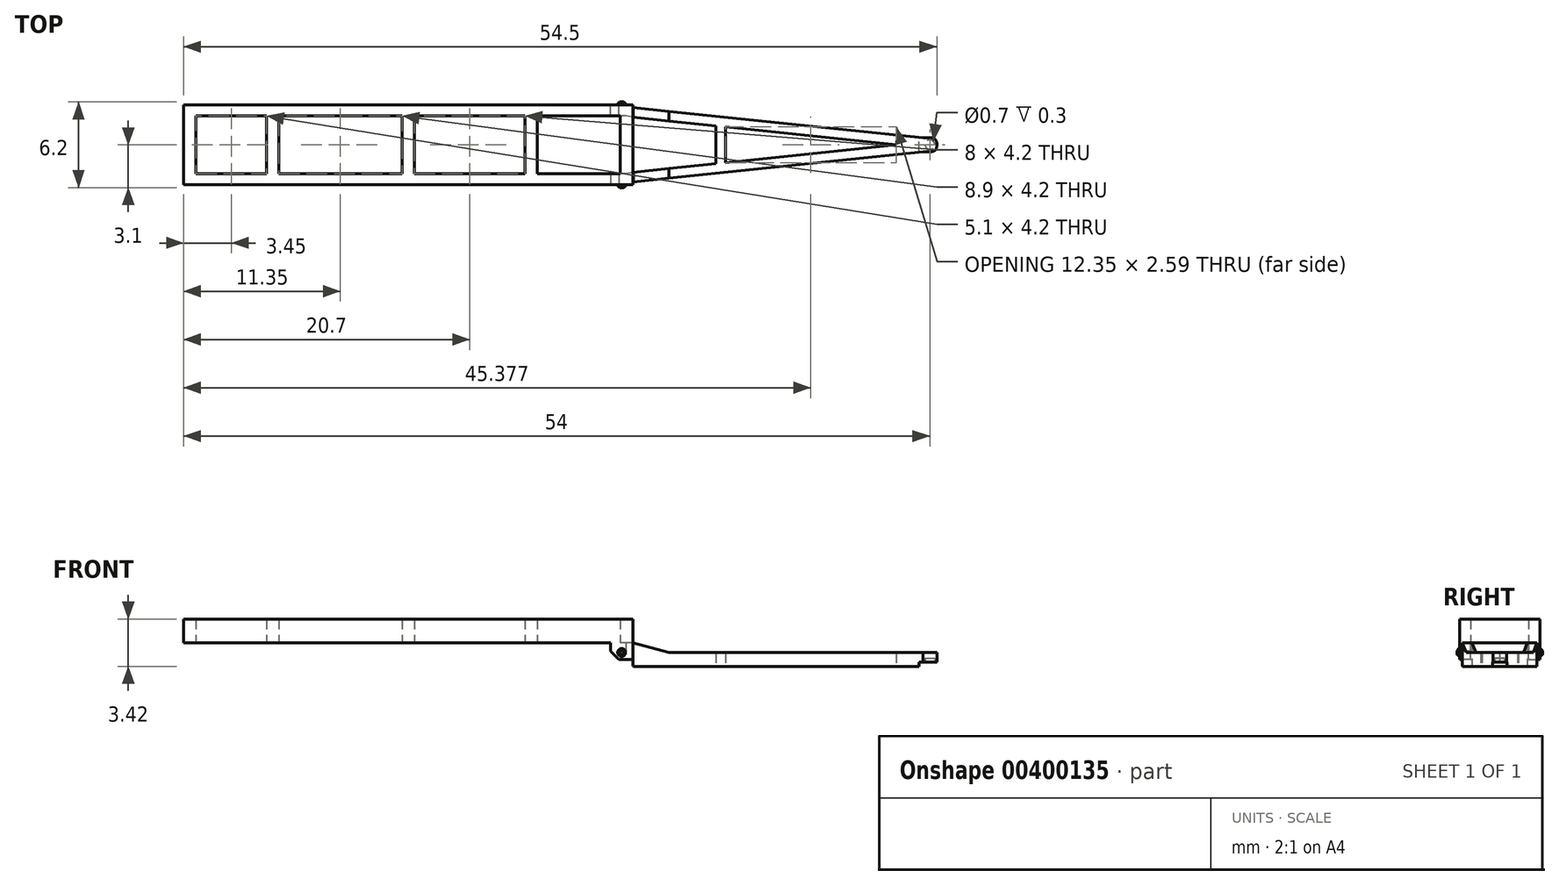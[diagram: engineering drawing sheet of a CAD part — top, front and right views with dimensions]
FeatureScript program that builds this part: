
annotation { "Feature Type Name" : "Feature", "Feature Type Description" : "" }
export const myFeature = defineFeature(function(context is Context, id is Id, definition is map)
    precondition{}
    {
        {
            var Q0;
            Q0=qCreatedBy(makeId("Top.planeOp"),FACE);
            var sketch = newSketch(context, id + "F0", { "sketchPlane" : qUnion([Q0])});
            skLineSegment(sketch, "E0", {"start": v(0, 0) * mm, "end": v(0, -2.9) * mm});
            skLineSegment(sketch, "E1", {"start": v(0, -2.9) * mm, "end": v(32.5, -2.9) * mm});
            skLineSegment(sketch, "E2", {"start": v(31.6, -2.1) * mm, "end": v(25.6, -2.1) * mm});
            skLineSegment(sketch, "E3", {"start": v(0.9, -2.1) * mm, "end": v(0.9, 0) * mm});
            skLineSegment(sketch, "E4", {"start": v(0.9, 0) * mm, "end": v(0, 0) * mm});
            skLineSegment(sketch, "E5", {"start": v(6, -2.1) * mm, "end": v(6, 0) * mm});
            skLineSegment(sketch, "E6", {"start": v(6, 0) * mm, "end": v(6.9, 0) * mm});
            skLineSegment(sketch, "E7", {"start": v(6.9, 0) * mm, "end": v(6.9, -2.1) * mm});
            skLineSegment(sketch, "E8.trimOffspring", {"start": v(6, -2.1) * mm, "end": v(0.9, -2.1) * mm});
            skLineSegment(sketch, "E9", {"start": v(32.5, -2.9) * mm, "end": v(32.5, 0) * mm});
            skLineSegment(sketch, "E10", {"start": v(32.5, 0) * mm, "end": v(31.6, 0) * mm});
            skLineSegment(sketch, "E11", {"start": v(31.6, 0) * mm, "end": v(31.6, -2.1) * mm});
            skLineSegment(sketch, "E12", {"start": v(25.6, -2.1) * mm, "end": v(25.6, 0) * mm});
            skLineSegment(sketch, "E13", {"start": v(25.6, 0) * mm, "end": v(24.7, 0) * mm});
            skLineSegment(sketch, "E14", {"start": v(24.7, 0) * mm, "end": v(24.7, -2.1) * mm});
            skLineSegment(sketch, "E15.trimOffspring", {"start": v(24.7, -2.1) * mm, "end": v(16.7, -2.1) * mm});
            skLineSegment(sketch, "E16", {"start": v(15.8, -2.1) * mm, "end": v(15.8, 0) * mm});
            skLineSegment(sketch, "E17", {"start": v(15.8, 0) * mm, "end": v(16.7, 0) * mm});
            skLineSegment(sketch, "E18", {"start": v(16.7, 0) * mm, "end": v(16.7, -2.1) * mm});
            skLineSegment(sketch, "E19.trimOffspring", {"start": v(15.8, -2.1) * mm, "end": v(6.9, -2.1) * mm});
            skSolve(sketch);
        }
        {
            var Q0;
            Q0 = qSketchRegion(id + "F0", true);
            extrude(context, id + "F1", {"entities" : qUnion([Q0]), "depth" : 1.72 * mm});
        }
        {
            var Q0;
            Q0=makeQuery(id+"F1.opExtrude","SWEPT_FACE",FACE,{"disambiguationData":[OSD([sQuery(id+"F0.wireOp",EDGE,"E1")])]});
            var sketch = newSketch(context, id + "F2", { "sketchPlane" : qUnion([Q0])});
            skLineSegment(sketch, "E20", {"start": v(30.9, -0.6) * mm, "end": v(32, -1.7) * mm});
            skLineSegment(sketch, "E21", {"start": v(32, -1.7) * mm, "end": v(32.5, -1.7) * mm});
            skLineSegment(sketch, "E22", {"start": v(32.5, -1.7) * mm, "end": v(32.5, 0) * mm});
            skLineSegment(sketch, "E23", {"start": v(32.5, 0) * mm, "end": v(30.9, 0) * mm});
            skLineSegment(sketch, "E24", {"start": v(30.9, 0) * mm, "end": v(30.9, -0.6) * mm});
            skSolve(sketch);
        }
        {
            var Q0;
            Q0 = qSketchRegion(id + "F2", true);
            var Q1;
            Q1=makeQuery(id+"F1.opExtrude","SWEPT_FACE",FACE,{"disambiguationData":[OSD([sQuery(id+"F0.wireOp",EDGE,"E2")])]});
            extrude(context, id + "F3", {"entities" : qUnion([Q0]), "operationType" : NewBodyOperationType.ADD, "endBound" : BoundingType.UP_TO_SURFACE, "oppositeDirection" : true, "endBoundEntityFace" : qUnion([Q1]), "depth" : 25 * mm});
        }
        {
            var Q0;
            Q0=makeQuery(id+"F3.opExtrude","SWEPT_FACE",FACE,{"disambiguationData":[OSD([sQuery(id+"F2.wireOp",EDGE,"E21")])]});
            var sketch = newSketch(context, id + "F4", { "sketchPlane" : qUnion([Q0])});
            skLineSegment(sketch, "E25", {"start": v(32.5, 2.7) * mm, "end": v(53.5, 0.5) * mm});
            skLineSegment(sketch, "E26", {"start": v(54.5, 0) * mm, "end": v(51.55, 0) * mm});
            skLineSegment(sketch, "E27", {"start": v(51.55, 0) * mm, "end": v(39.2, 1.3) * mm});
            skLineSegment(sketch, "E28", {"start": v(32.5, 2.1) * mm, "end": v(32.5, 2.7) * mm});
            skLineSegment(sketch, "E29", {"start": v(32.5, 2.1) * mm, "end": v(32, 2.1) * mm});
            skLineSegment(sketch, "E30", {"start": v(32, 2.1) * mm, "end": v(32.5, 2) * mm});
            skLineSegment(sketch, "E31", {"start": v(38.5, 1.37) * mm, "end": v(38.5, 0) * mm});
            skLineSegment(sketch, "E32", {"start": v(38.5, 0) * mm, "end": v(39.2, 0) * mm});
            skLineSegment(sketch, "E33", {"start": v(39.2, 0) * mm, "end": v(39.2, 1.3) * mm});
            skLineSegment(sketch, "E34.trimOffspring", {"start": v(38.5, 1.37) * mm, "end": v(32.5, 2) * mm});
            skLineSegment(sketch, "E35", {"start": v(53.5, 0.5) * mm, "end": v(54.5, 0.5) * mm});
            skLineSegment(sketch, "E36", {"start": v(54.5, 0.5) * mm, "end": v(54.5, 0) * mm});
            skSolve(sketch);
        }
        {
            var Q0;
            Q0 = qSketchRegion(id + "F4", true);
            extrude(context, id + "F5", {"entities" : qUnion([Q0]), "operationType" : NewBodyOperationType.ADD, "oppositeDirection" : true, "depth" : 2 * mm, "offsetDistance" : 25 * mm});
        }
        {
            var Q0;
            Q0=makeQuery(id+"F3.boolean.opBoolean","MERGE",FACE,{"derivedFrom":[makeQuery(id+"F1.opExtrude","SWEPT_FACE",FACE,{"disambiguationData":[OSD([sQuery(id+"F0.wireOp",EDGE,"E1")])]}),makeQuery(id+"F3.opExtrude","CAP_FACE",FACE,{"disambiguationData":[OSD([sQuery(id+"F2.wireOp",EDGE,"E20"),sQuery(id+"F2.wireOp",EDGE,"E21"),sQuery(id+"F2.wireOp",EDGE,"E22"),sQuery(id+"F2.wireOp",EDGE,"E23"),sQuery(id+"F2.wireOp",EDGE,"E24")])],"isStart":true})]});
            var sketch = newSketch(context, id + "F6", { "sketchPlane" : qUnion([Q0])});
            skLineSegment(sketch, "E37.0", {"start": v(32.5, 0.3) * mm, "end": v(32.5, -1.2) * mm});
            skLineSegment(sketch, "E38.0", {"start": v(54.5, 0.3) * mm, "end": v(54.5, -0.7) * mm});
            skLineSegment(sketch, "E39", {"start": v(32.5, 0.3) * mm, "end": v(54.5, 0.3) * mm});
            skLineSegment(sketch, "E40", {"start": v(32.5, 0) * mm, "end": v(35.11, -0.7) * mm});
            skLineSegment(sketch, "E41", {"start": v(35.11, -0.7) * mm, "end": v(54.5, -0.7) * mm});
            skLineSegment(sketch, "E42", {"start": v(32.5, -1.67) * mm, "end": v(32.6, -1.7) * mm});
            skLineSegment(sketch, "E43.0", {"start": v(32.5, -1.7) * mm, "end": v(32.6, -1.7) * mm});
            skLineSegment(sketch, "E44", {"start": v(32.5, -1.2) * mm, "end": v(32.5, -1.67) * mm});
            skLineSegment(sketch, "E45", {"start": v(32.5, -1.2) * mm, "end": v(31.5, -1.2) * mm});
            skLineSegment(sketch, "E46", {"start": v(31.5, -1.2) * mm, "end": v(32, -1.7) * mm});
            skLineSegment(sketch, "E47", {"start": v(32, -1.7) * mm, "end": v(32.5, -1.7) * mm});
            skPoint(sketch, "E48.orphan", {"position": v(53.5, -1.7) * mm});
            skPoint(sketch, "E49.orphan", {"position": v(54.5, -1.7) * mm});
            skSolve(sketch);
        }
        {
            var Q0;
            Q0 = qSketchRegion(id + "F6", true);
            extrude(context, id + "F7", {"entities" : qUnion([Q0]), "operationType" : NewBodyOperationType.REMOVE, "endBound" : BoundingType.THROUGH_ALL, "oppositeDirection" : true, "depth" : 25 * mm});
        }
        {
            var Q0;
            Q0=makeQuery(id+"F3.boolean.opBoolean","MERGE",FACE,{"derivedFrom":[makeQuery(id+"F1.opExtrude","SWEPT_FACE",FACE,{"disambiguationData":[OSD([sQuery(id+"F0.wireOp",EDGE,"E1")])]}),makeQuery(id+"F3.opExtrude","CAP_FACE",FACE,{"disambiguationData":[OSD([sQuery(id+"F2.wireOp",EDGE,"E20"),sQuery(id+"F2.wireOp",EDGE,"E21"),sQuery(id+"F2.wireOp",EDGE,"E22"),sQuery(id+"F2.wireOp",EDGE,"E23"),sQuery(id+"F2.wireOp",EDGE,"E24")])],"isStart":true})]});
            var sketch = newSketch(context, id + "F8", { "sketchPlane" : qUnion([Q0])});
            skCircle(sketch, "E50", {"center": v(31.7, -0.7) * mm, "radius": 0.29 * mm});
            skSolve(sketch);
        }
        {
            var Q0;
            Q0 = qSketchRegion(id + "F8", true);
            extrude(context, id + "F9", {"entities" : qUnion([Q0]), "operationType" : NewBodyOperationType.ADD, "depth" : 0.2 * mm});
        }
        {
            var Q0;
            Q0=makeQuery(id+"F9.opExtrude","CAP_EDGE",EDGE,{"disambiguationData":[OSD([sQuery(id+"F8.wireOp",EDGE,"E50")])],"isStart":false});
            chamfer(context, id + "F10", {"entities" : qUnion([Q0]), "width" : 0.15 * mm, "tangentPropagation" : true});
        }
        {
            var Q0;
            Q0=makeQuery(id+"F1.opExtrude","SWEPT_BODY",BODY,{"disambiguationData":[OSD([sQuery(id+"F0.wireOp",EDGE,"E0"),sQuery(id+"F0.wireOp",EDGE,"E1"),sQuery(id+"F0.wireOp",EDGE,"E2"),sQuery(id+"F0.wireOp",EDGE,"E3"),sQuery(id+"F0.wireOp",EDGE,"E4"),sQuery(id+"F0.wireOp",EDGE,"E5"),sQuery(id+"F0.wireOp",EDGE,"E6"),sQuery(id+"F0.wireOp",EDGE,"E7"),sQuery(id+"F0.wireOp",EDGE,"E8.trimOffspring"),sQuery(id+"F0.wireOp",EDGE,"E9"),sQuery(id+"F0.wireOp",EDGE,"E10"),sQuery(id+"F0.wireOp",EDGE,"E11"),sQuery(id+"F0.wireOp",EDGE,"E12"),sQuery(id+"F0.wireOp",EDGE,"E13"),sQuery(id+"F0.wireOp",EDGE,"E14"),sQuery(id+"F0.wireOp",EDGE,"E15.trimOffspring"),sQuery(id+"F0.wireOp",EDGE,"E16"),sQuery(id+"F0.wireOp",EDGE,"E17"),sQuery(id+"F0.wireOp",EDGE,"E18"),sQuery(id+"F0.wireOp",EDGE,"E19.trimOffspring")])]});
            var Q1;
            Q1=makeQuery(id+"F1.opExtrude","SWEPT_FACE",FACE,{"disambiguationData":[OSD([sQuery(id+"F0.wireOp",EDGE,"E17")])]});
            mirror(context, id + "F11", {"operationType" : NewBodyOperationType.ADD, "entities" : qUnion([Q0]), "mirrorPlane" : qUnion([Q1])});
        }
        {
            var Q0;
            Q0=makeQuery(id+"F11.opPattern","COPY",FACE,{"derivedFrom":makeQuery(id+"F3.boolean.opBoolean","MERGE",FACE,{"derivedFrom":[makeQuery(id+"F1.opExtrude","SWEPT_FACE",FACE,{"disambiguationData":[OSD([sQuery(id+"F0.wireOp",EDGE,"E1")])]}),makeQuery(id+"F3.opExtrude","CAP_FACE",FACE,{"disambiguationData":[OSD([sQuery(id+"F2.wireOp",EDGE,"E20"),sQuery(id+"F2.wireOp",EDGE,"E21"),sQuery(id+"F2.wireOp",EDGE,"E22"),sQuery(id+"F2.wireOp",EDGE,"E23")])],"isStart":true})]}),"instanceName":"1"});
            var sketch = newSketch(context, id + "F12", { "sketchPlane" : qUnion([Q0])});
            skLineSegment(sketch, "E51.bottom", {"start": v(-54.5, -1.7) * mm, "end": v(-53.2, -1.7) * mm});
            skLineSegment(sketch, "E51.top", {"start": v(-54.5, -1.4) * mm, "end": v(-53.2, -1.4) * mm});
            skLineSegment(sketch, "E51.left", {"start": v(-54.5, -1.7) * mm, "end": v(-54.5, -1.4) * mm});
            skLineSegment(sketch, "E51.right", {"start": v(-53.2, -1.7) * mm, "end": v(-53.2, -1.4) * mm});
            skSolve(sketch);
        }
        {
            var Q0;
            Q0 = qSketchRegion(id + "F12", true);
            extrude(context, id + "F13", {"entities" : qUnion([Q0]), "operationType" : NewBodyOperationType.REMOVE, "endBound" : BoundingType.THROUGH_ALL, "oppositeDirection" : true, "depth" : 25 * mm});
        }
        {
            var Q0;
            Q0=makeQuery(id+"F11.opPattern","COPY",EDGE,{"derivedFrom":makeQuery(id+"F5.opExtrude","SWEPT_EDGE",EDGE,{"disambiguationData":[OSD([sQuery(id+"F4.wireOp",EDGE,"E35"),sQuery(id+"F4.wireOp",EDGE,"E36")])]}),"instanceName":"1"});
            var Q1;
            Q1=makeQuery(id+"F5.opExtrude","SWEPT_EDGE",EDGE,{"disambiguationData":[OSD([sQuery(id+"F4.wireOp",EDGE,"E35"),sQuery(id+"F4.wireOp",EDGE,"E36")])]});
            fillet(context, id + "F14", {"entities" : qUnion([Q0, Q1]), "radius" : 0.4 * mm, "tangentPropagation" : true, "allowEdgeOverflow" : false});
        }
        {
            var Q0;
            Q0=makeQuery(id+"F13.boolean.opBoolean","COPY",FACE,{"derivedFrom":makeQuery(id+"F13.opExtrude","SWEPT_FACE",FACE,{"disambiguationData":[OSD([sQuery(id+"F12.wireOp",EDGE,"E51.top")])]})});
            var sketch = newSketch(context, id + "F15", { "sketchPlane" : qUnion([Q0])});
            skCircle(sketch, "E52", {"center": v(54, 0) * mm, "radius": 0.35 * mm});
            skPoint(sketch, "E53", {"position": v(54.5, 0) * mm});
            skSolve(sketch);
        }
        {
            var Q0;
            Q0 = qSketchRegion(id + "F15", true);
            extrude(context, id + "F16", {"entities" : qUnion([Q0]), "operationType" : NewBodyOperationType.REMOVE, "oppositeDirection" : true, "depth" : 0.3 * mm});
        }
    });
